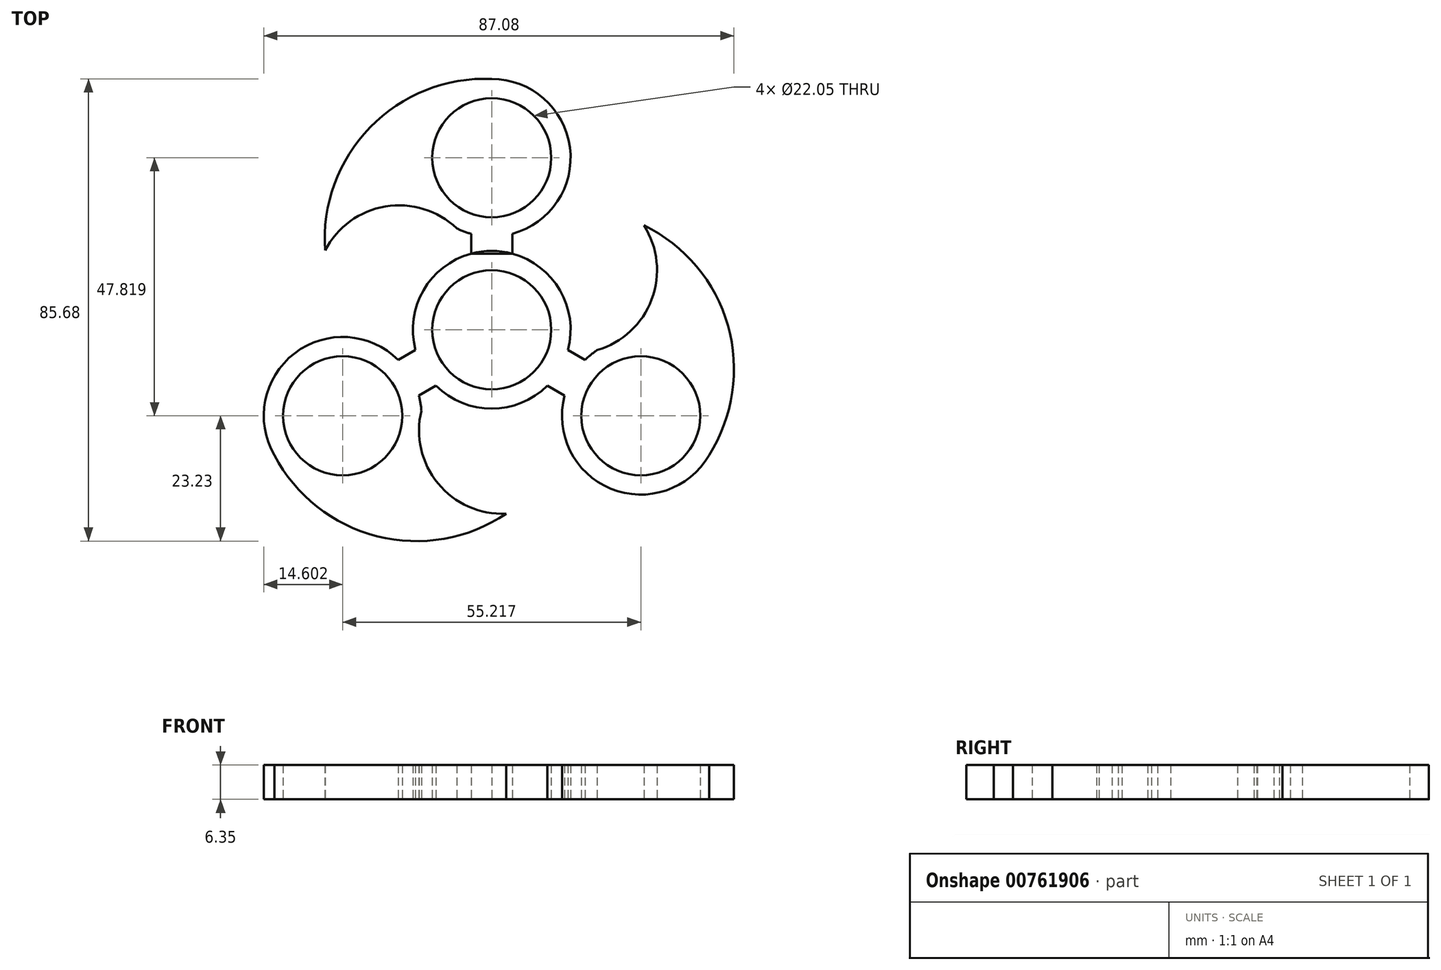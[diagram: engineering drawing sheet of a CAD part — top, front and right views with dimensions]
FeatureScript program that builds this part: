
annotation { "Feature Type Name" : "Feature", "Feature Type Description" : "" }
export const myFeature = defineFeature(function(context is Context, id is Id, definition is map)
    precondition{}
    {
        {
            var Q0;
            Q0=qCreatedBy(makeId("Top.planeOp"),FACE);
            var sketch = newSketch(context, id + "F0", { "sketchPlane" : qUnion([Q0])});
            skCircle(sketch, "E0", {"center": v(0, 0) * mm, "radius": 14.6 * mm});
            skCircle(sketch, "E1", {"center": v(0, 0) * mm, "radius": 11.02 * mm});
            skLineSegment(sketch, "E2", {"start": v(-3.8, 14.1) * mm, "end": v(-3.81, 31.88) * mm});
            skLineSegment(sketch, "E3", {"start": v(-3.81, 31.88) * mm, "end": v(3.81, 31.88) * mm});
            skLineSegment(sketch, "E4", {"start": v(3.8, 31.88) * mm, "end": v(3.81, 14.1) * mm});
            skLineSegment(sketch, "E5", {"start": v(3.8, 14.1) * mm, "end": v(-3.8, 14.1) * mm});
            skCircle(sketch, "E6", {"center": v(0, 31.88) * mm, "radius": 14.6 * mm});
            skCircle(sketch, "E7", {"center": v(0, 31.88) * mm, "radius": 11.02 * mm});
            skArc(sketch, "E8", {"start": v(0, 46.48) * mm, "mid": v(-22.53, 37.5) * mm, "end": v(-30.86, 14.73) * mm});
            skArc(sketch, "E9", {"start": v(-6.49, 18.8) * mm, "mid": v(-19.69, 22.85) * mm, "end": v(-30.86, 14.73) * mm});
            skArc(sketch, "E10.1.0", {"start": v(-40.26, -23.24) * mm, "mid": v(-21.22, -38.26) * mm, "end": v(2.67, -34.09) * mm});
            skCircle(sketch, "E10.1.1", {"center": v(-27.6, -15.94) * mm, "radius": 14.6 * mm});
            skCircle(sketch, "E10.1.2", {"center": v(-27.6, -15.94) * mm, "radius": 11.02 * mm});
            skLineSegment(sketch, "E10.1.3", {"start": v(-10.3, -10.35) * mm, "end": v(-25.7, -19.24) * mm});
            skLineSegment(sketch, "E10.1.4", {"start": v(-29.51, -12.64) * mm, "end": v(-14.12, -3.75) * mm});
            skArc(sketch, "E10.2.0", {"start": v(40.26, -23.24) * mm, "mid": v(43.74, 0.76) * mm, "end": v(28.19, 19.36) * mm});
            skCircle(sketch, "E10.2.1", {"center": v(27.6, -15.94) * mm, "radius": 14.6 * mm});
            skCircle(sketch, "E10.2.2", {"center": v(27.6, -15.94) * mm, "radius": 11.02 * mm});
            skLineSegment(sketch, "E10.2.3", {"start": v(14.12, -3.75) * mm, "end": v(29.51, -12.64) * mm});
            skLineSegment(sketch, "E10.2.4", {"start": v(25.7, -19.24) * mm, "end": v(10.3, -10.35) * mm});
            skArc(sketch, "E11.1.0", {"start": v(-13.03, -15.02) * mm, "mid": v(-9.94, -28.47) * mm, "end": v(2.67, -34.09) * mm});
            skArc(sketch, "E11.2.0", {"start": v(19.52, -3.78) * mm, "mid": v(29.63, 5.63) * mm, "end": v(28.19, 19.36) * mm});
            skSolve(sketch);
        }
        {
            var Q0;
            {var subQ0=sQuery(id+"F0.wireOp",EDGE,"E8");Q0=makeQuery(id+"F0.imprint","IMPRINT",FACE,{"disambiguationData":[TD([[makeQuery(id+"F0.imprint","IMPRINT",EDGE,{"derivedFrom":subQ0}),1.0]])]});}
            var Q1;
            {var subQ0=sQuery(id+"F0.wireOp",EDGE,"E6");var subQ5=sQuery(id+"F0.wireOp",EDGE,"E2");var subQ6=makeQuery(id+"F0.imprint","INTERSECT",VERTEX,{"derivedFrom":[subQ5,subQ0]});Q1=makeQuery(id+"F0.imprint","IMPRINT",FACE,{"disambiguationData":[TD([[makeQuery(id+"F0.imprint","IMPRINT",EDGE,{"disambiguationData":[TD([[subQ6,-1.0]])],"derivedFrom":subQ5}),1.0]])]});}
            var Q2;
            {var subQ0=sQuery(id+"F0.wireOp",EDGE,"E6");var subQ1=sQuery(id+"F0.wireOp",EDGE,"E2");var subQ2=makeQuery(id+"F0.imprint","INTERSECT",VERTEX,{"derivedFrom":[subQ1,subQ0]});Q2=makeQuery(id+"F0.imprint","IMPRINT",FACE,{"disambiguationData":[TD([[makeQuery(id+"F0.imprint","IMPRINT",EDGE,{"disambiguationData":[TD([[subQ2,-1.0]])],"derivedFrom":subQ1}),-1.0]])]});}
            var Q3;
            {var subQ1=sQuery(id+"F0.wireOp",EDGE,"E2");var subQ6=sQuery(id+"F0.wireOp",EDGE,"E6");var subQ7=makeQuery(id+"F0.imprint","INTERSECT",VERTEX,{"derivedFrom":[subQ1,subQ6]});Q3=makeQuery(id+"F0.imprint","IMPRINT",FACE,{"disambiguationData":[TD([[makeQuery(id+"F0.imprint","IMPRINT",EDGE,{"disambiguationData":[TD([[subQ7,-1.0]])],"derivedFrom":subQ6}),-1.0]])]});}
            var Q4;
            Q4=makeQuery(id+"F0.imprint","IMPRINT",FACE,{"disambiguationData":[TD([[makeQuery(id+"F0.imprint","IMPRINT",EDGE,{"derivedFrom":sQuery(id+"F0.wireOp",EDGE,"E1")}),-1.0]])]});
            var Q5;
            {var subQ5=sQuery(id+"F0.wireOp",EDGE,"E10.1.1");var subQ6=makeQuery(id+"F0.imprint","INTERSECT",VERTEX,{"derivedFrom":[sQuery(id+"F0.wireOp",EDGE,"E10.1.0"),subQ5]});Q5=makeQuery(id+"F0.imprint","IMPRINT",FACE,{"disambiguationData":[TD([[makeQuery(id+"F0.imprint","IMPRINT",EDGE,{"disambiguationData":[TD([[subQ6,-1.0]])],"derivedFrom":subQ5}),1.0]])]});}
            var Q6;
            {var subQ0=sQuery(id+"F0.wireOp",EDGE,"E10.1.3");var subQ1=sQuery(id+"F0.wireOp",EDGE,"E10.1.1");var subQ2=makeQuery(id+"F0.imprint","INTERSECT",VERTEX,{"derivedFrom":[subQ1,subQ0]});Q6=makeQuery(id+"F0.imprint","IMPRINT",FACE,{"disambiguationData":[TD([[makeQuery(id+"F0.imprint","IMPRINT",EDGE,{"disambiguationData":[TD([[subQ2,-1.0]])],"derivedFrom":subQ1}),1.0]])]});}
            var Q7;
            {var subQ0=sQuery(id+"F0.wireOp",EDGE,"E10.1.3");var subQ1=sQuery(id+"F0.wireOp",EDGE,"E0");var subQ2=makeQuery(id+"F0.imprint","INTERSECT",VERTEX,{"derivedFrom":[subQ1,subQ0]});Q7=makeQuery(id+"F0.imprint","IMPRINT",FACE,{"disambiguationData":[TD([[makeQuery(id+"F0.imprint","IMPRINT",EDGE,{"disambiguationData":[TD([[subQ2,1.0]])],"derivedFrom":subQ1}),-1.0]])]});}
            var Q8;
            {var subQ0=sQuery(id+"F0.wireOp",EDGE,"E10.1.0");Q8=makeQuery(id+"F0.imprint","IMPRINT",FACE,{"disambiguationData":[TD([[makeQuery(id+"F0.imprint","IMPRINT",EDGE,{"derivedFrom":subQ0}),1.0]])]});}
            var Q9;
            {var subQ0=sQuery(id+"F0.wireOp",EDGE,"E10.2.3");var subQ1=sQuery(id+"F0.wireOp",EDGE,"E0");var subQ2=makeQuery(id+"F0.imprint","INTERSECT",VERTEX,{"derivedFrom":[subQ1,subQ0]});Q9=makeQuery(id+"F0.imprint","IMPRINT",FACE,{"disambiguationData":[TD([[makeQuery(id+"F0.imprint","IMPRINT",EDGE,{"disambiguationData":[TD([[subQ2,1.0]])],"derivedFrom":subQ1}),-1.0]])]});}
            var Q10;
            {var subQ5=sQuery(id+"F0.wireOp",EDGE,"E10.2.1");var subQ6=makeQuery(id+"F0.imprint","INTERSECT",VERTEX,{"derivedFrom":[sQuery(id+"F0.wireOp",EDGE,"E10.2.0"),subQ5]});Q10=makeQuery(id+"F0.imprint","IMPRINT",FACE,{"disambiguationData":[TD([[makeQuery(id+"F0.imprint","IMPRINT",EDGE,{"disambiguationData":[TD([[subQ6,-1.0]])],"derivedFrom":subQ5}),1.0]])]});}
            var Q11;
            {var subQ0=sQuery(id+"F0.wireOp",EDGE,"E10.2.3");var subQ1=sQuery(id+"F0.wireOp",EDGE,"E10.2.1");var subQ2=makeQuery(id+"F0.imprint","INTERSECT",VERTEX,{"derivedFrom":[subQ1,subQ0]});Q11=makeQuery(id+"F0.imprint","IMPRINT",FACE,{"disambiguationData":[TD([[makeQuery(id+"F0.imprint","IMPRINT",EDGE,{"disambiguationData":[TD([[subQ2,-1.0]])],"derivedFrom":subQ1}),1.0]])]});}
            var Q12;
            {var subQ0=sQuery(id+"F0.wireOp",EDGE,"E10.2.0");Q12=makeQuery(id+"F0.imprint","IMPRINT",FACE,{"disambiguationData":[TD([[makeQuery(id+"F0.imprint","IMPRINT",EDGE,{"derivedFrom":subQ0}),1.0]])]});}
            extrude(context, id + "F1", {"entities" : qUnion([Q0, Q1, Q2, Q3, Q4, Q5, Q6, Q7, Q8, Q9, Q10, Q11, Q12]), "depth" : 6.35 * mm, "offsetDistance" : 25.4 * mm});
        }
    });
